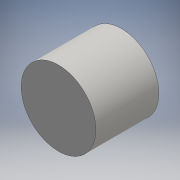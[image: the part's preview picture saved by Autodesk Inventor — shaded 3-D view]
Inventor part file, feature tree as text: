
AUTODESK INVENTOR PART (.ipt)
format: ipt  version: 2016 (Build 200138000, 138)  size: 88,064 bytes
history: native  units: mm
features: other x1, extrude x1, sketch x1
ambient origin geometry x8: Origin, YZ Plane, XZ Plane, XY Plane, X Axis, Y Axis, Z Axis, Center Point
bodies: Body1 (feature_tree)
feature tree (3):
  other  "ソリッド1"
  extrude  "押し出し1"  Depth=38.0mm
  sketch  "スケッチ1"
